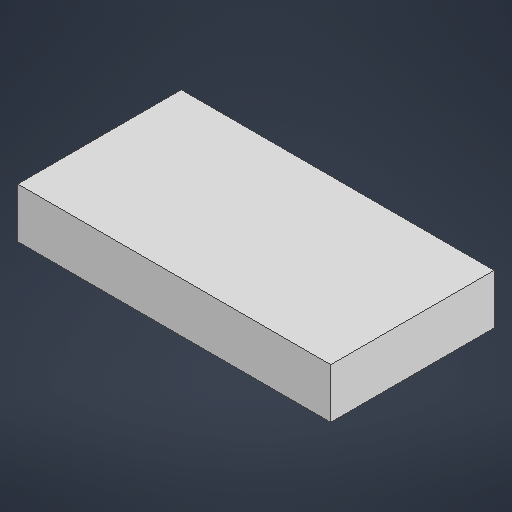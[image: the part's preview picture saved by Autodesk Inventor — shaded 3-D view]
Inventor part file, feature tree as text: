
AUTODESK INVENTOR PART (.ipt)
format: ipt  version: 2025.2 (Build 292293000, 293)  size: 165,888 bytes
history: native  units: mm
features: extrude x1, sketch x1
ambient origin geometry x8: Origin, YZ Plane, XZ Plane, XY Plane, X Axis, Y Axis, Z Axis, Center Point
bodies: Solid1 (feature_tree)
feature tree (2):
  extrude  "Extrusion1"  Depth=65.5mm
  sketch  "Sketch1"  dims[d0=125.4mm d1=65.5mm d2=20.0mm d3=0.0mm]
